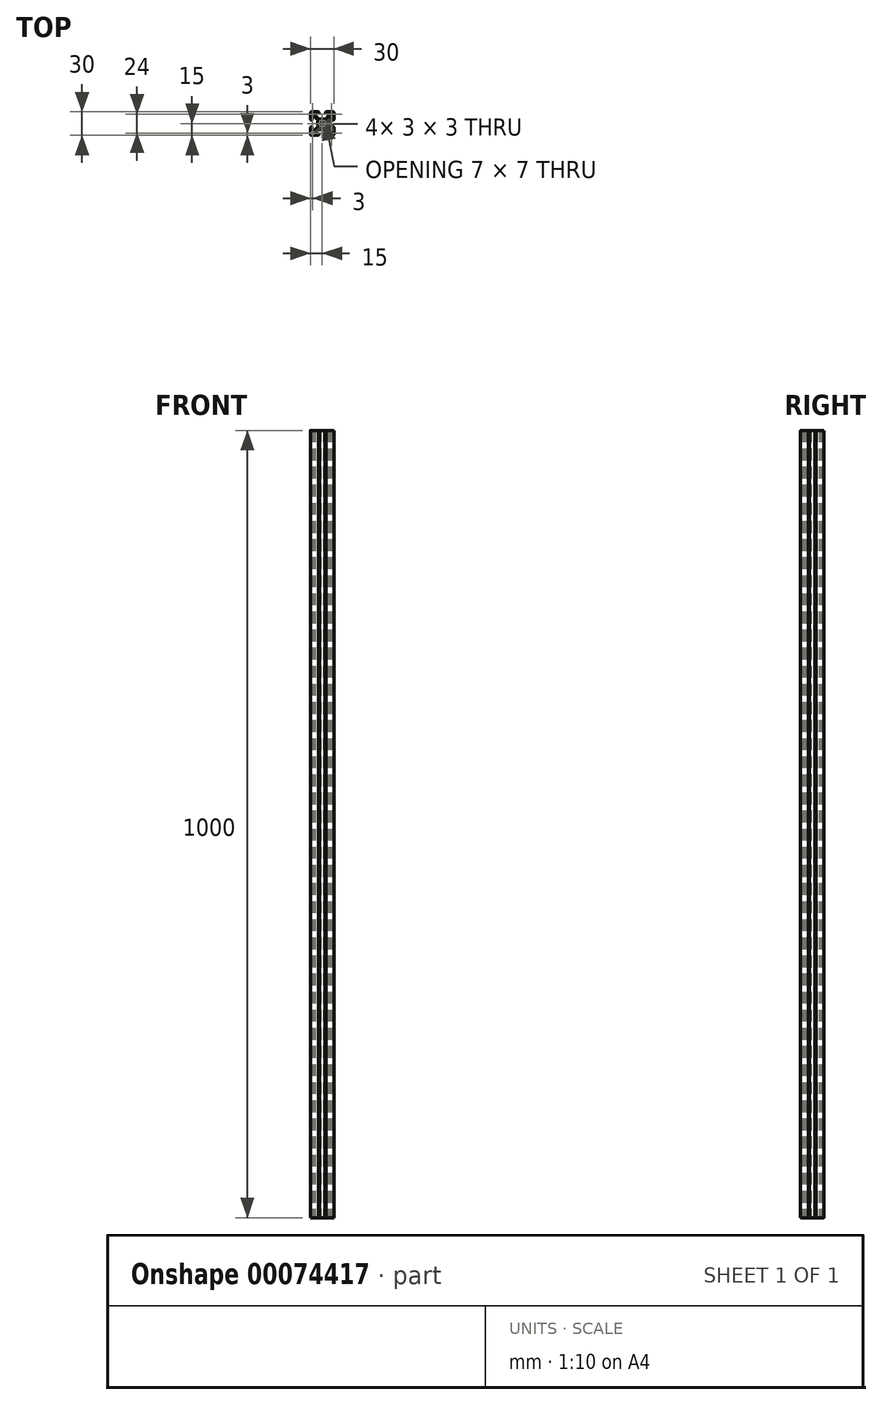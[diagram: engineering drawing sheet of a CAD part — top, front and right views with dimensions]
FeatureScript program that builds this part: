
annotation { "Feature Type Name" : "Feature", "Feature Type Description" : "" }
export const myFeature = defineFeature(function(context is Context, id is Id, definition is map)
    precondition{}
    {
        {
            var Q0;
            Q0=qCreatedBy(makeId("Top.planeOp"),FACE);
            var sketch = newSketch(context, id + "F0", { "sketchPlane" : qUnion([Q0])});
            skCircle(sketch, "E0", {"center": v(0, 0) * mm, "radius": 3.5 * mm});
            skLineSegment(sketch, "E1.bottom", {"start": v(-15, 15) * mm, "end": v(15, 15) * mm});
            skLineSegment(sketch, "E1.top", {"start": v(-15, -15) * mm, "end": v(15, -15) * mm});
            skLineSegment(sketch, "E1.left", {"start": v(-15, 15) * mm, "end": v(-15, -15) * mm});
            skLineSegment(sketch, "E1.right", {"start": v(15, 15) * mm, "end": v(15, -15) * mm});
            skLineSegment(sketch, "E2", {"start": v(-12.8, 12.8) * mm, "end": v(12.8, 12.8) * mm, "construction": true});
            skLineSegment(sketch, "E3", {"start": v(12.8, 12.8) * mm, "end": v(12.8, -12.8) * mm, "construction": true});
            skLineSegment(sketch, "E4", {"start": v(12.8, -12.8) * mm, "end": v(-12.8, -12.8) * mm, "construction": true});
            skLineSegment(sketch, "E5", {"start": v(-12.8, -12.8) * mm, "end": v(-12.8, 12.8) * mm, "construction": true});
            skLineSegment(sketch, "E6", {"start": v(-15, -15) * mm, "end": v(15, 15) * mm, "construction": true});
            skLineSegment(sketch, "E7", {"start": v(-15, 15) * mm, "end": v(15, -15) * mm, "construction": true});
            skLineSegment(sketch, "E8", {"start": v(-13.44, 15) * mm, "end": v(15, -13.44) * mm, "construction": true});
            skLineSegment(sketch, "E9", {"start": v(-15, 13.44) * mm, "end": v(13.44, -15) * mm, "construction": true});
            skLineSegment(sketch, "E10", {"start": v(13.44, 15) * mm, "end": v(-15, -13.44) * mm, "construction": true});
            skLineSegment(sketch, "E11", {"start": v(-13.44, -15) * mm, "end": v(15, 13.44) * mm, "construction": true});
            skLineSegment(sketch, "E12", {"start": v(-15, 4.1) * mm, "end": v(15, 4.1) * mm, "construction": true});
            skPoint(sketch, "E13.endSnap0", {"position": v(0.78, -0.78) * mm});
            skLineSegment(sketch, "E14", {"start": v(-4.1, 15) * mm, "end": v(-4.1, -15) * mm, "construction": true});
            skLineSegment(sketch, "E15", {"start": v(4.1, -15) * mm, "end": v(4.1, 15) * mm, "construction": true});
            skLineSegment(sketch, "E16", {"start": v(-15, -4.1) * mm, "end": v(15, -4.1) * mm, "construction": true});
            skLineSegment(sketch, "E17", {"start": v(-13.5, 13.5) * mm, "end": v(13.5, 13.5) * mm, "construction": true});
            skLineSegment(sketch, "E18", {"start": v(13.5, 13.5) * mm, "end": v(13.5, -13.5) * mm, "construction": true});
            skLineSegment(sketch, "E19", {"start": v(13.5, -13.5) * mm, "end": v(-13.5, -13.5) * mm, "construction": true});
            skLineSegment(sketch, "E20", {"start": v(-13.5, -13.5) * mm, "end": v(-13.5, 13.5) * mm, "construction": true});
            skLineSegment(sketch, "E21.bottom", {"start": v(-13.5, 13.5) * mm, "end": v(-10.5, 13.5) * mm});
            skLineSegment(sketch, "E21.top", {"start": v(-13.5, 10.5) * mm, "end": v(-10.5, 10.5) * mm});
            skLineSegment(sketch, "E21.left", {"start": v(-13.5, 13.5) * mm, "end": v(-13.5, 10.5) * mm});
            skLineSegment(sketch, "E21.right", {"start": v(-10.5, 13.5) * mm, "end": v(-10.5, 10.5) * mm});
            skLineSegment(sketch, "E22.bottom", {"start": v(13.5, 13.5) * mm, "end": v(10.5, 13.5) * mm});
            skLineSegment(sketch, "E22.top", {"start": v(13.5, 10.5) * mm, "end": v(10.5, 10.5) * mm});
            skLineSegment(sketch, "E22.left", {"start": v(13.5, 13.5) * mm, "end": v(13.5, 10.5) * mm});
            skLineSegment(sketch, "E22.right", {"start": v(10.5, 13.5) * mm, "end": v(10.5, 10.5) * mm});
            skLineSegment(sketch, "E23.bottom", {"start": v(13.5, -13.5) * mm, "end": v(10.5, -13.5) * mm});
            skLineSegment(sketch, "E23.top", {"start": v(13.5, -10.5) * mm, "end": v(10.5, -10.5) * mm});
            skLineSegment(sketch, "E23.left", {"start": v(13.5, -13.5) * mm, "end": v(13.5, -10.5) * mm});
            skLineSegment(sketch, "E23.right", {"start": v(10.5, -13.5) * mm, "end": v(10.5, -10.5) * mm});
            skLineSegment(sketch, "E24.bottom", {"start": v(-13.5, -13.5) * mm, "end": v(-10.5, -13.5) * mm});
            skLineSegment(sketch, "E24.top", {"start": v(-13.5, -10.5) * mm, "end": v(-10.5, -10.5) * mm});
            skLineSegment(sketch, "E24.left", {"start": v(-13.5, -13.5) * mm, "end": v(-13.5, -10.5) * mm});
            skLineSegment(sketch, "E24.right", {"start": v(-10.5, -13.5) * mm, "end": v(-10.5, -10.5) * mm});
            skLineSegment(sketch, "E25.bottom", {"start": v(13.5, 13.5) * mm, "end": v(9, 13.5) * mm, "construction": true});
            skLineSegment(sketch, "E25.top", {"start": v(13.5, 9) * mm, "end": v(9, 9) * mm, "construction": true});
            skLineSegment(sketch, "E25.left", {"start": v(13.5, 13.5) * mm, "end": v(13.5, 9) * mm, "construction": true});
            skLineSegment(sketch, "E25.right", {"start": v(9, 13.5) * mm, "end": v(9, 9) * mm, "construction": true});
            skLineSegment(sketch, "E26.bottom", {"start": v(-13.5, 13.5) * mm, "end": v(-9, 13.5) * mm, "construction": true});
            skLineSegment(sketch, "E26.top", {"start": v(-13.5, 9) * mm, "end": v(-9, 9) * mm, "construction": true});
            skLineSegment(sketch, "E26.left", {"start": v(-13.5, 13.5) * mm, "end": v(-13.5, 9) * mm, "construction": true});
            skLineSegment(sketch, "E26.right", {"start": v(-9, 13.5) * mm, "end": v(-9, 9) * mm, "construction": true});
            skLineSegment(sketch, "E27.bottom", {"start": v(-13.5, -13.5) * mm, "end": v(-9, -13.5) * mm, "construction": true});
            skLineSegment(sketch, "E27.top", {"start": v(-13.5, -9) * mm, "end": v(-9, -9) * mm, "construction": true});
            skLineSegment(sketch, "E27.left", {"start": v(-13.5, -13.5) * mm, "end": v(-13.5, -9) * mm, "construction": true});
            skLineSegment(sketch, "E27.right", {"start": v(-9, -13.5) * mm, "end": v(-9, -9) * mm, "construction": true});
            skLineSegment(sketch, "E28.bottom", {"start": v(13.5, -13.5) * mm, "end": v(9, -13.5) * mm, "construction": true});
            skLineSegment(sketch, "E28.top", {"start": v(13.5, -9) * mm, "end": v(9, -9) * mm, "construction": true});
            skLineSegment(sketch, "E28.left", {"start": v(13.5, -13.5) * mm, "end": v(13.5, -9) * mm, "construction": true});
            skLineSegment(sketch, "E28.right", {"start": v(9, -13.5) * mm, "end": v(9, -9) * mm, "construction": true});
            skCircle(sketch, "E29", {"center": v(0, 0) * mm, "radius": 6 * mm, "construction": true});
            skLineSegment(sketch, "E30", {"start": v(15, 4.1) * mm, "end": v(13.5, 4.1) * mm});
            skLineSegment(sketch, "E31", {"start": v(15, -4.1) * mm, "end": v(13.5, -4.1) * mm});
            skLineSegment(sketch, "E32", {"start": v(3.4, -4.95) * mm, "end": v(9, -10.56) * mm});
            skLineSegment(sketch, "E33", {"start": v(9, -10.56) * mm, "end": v(9, -12.8) * mm});
            skLineSegment(sketch, "E34", {"start": v(9, -12.8) * mm, "end": v(4.1, -12.8) * mm});
            skLineSegment(sketch, "E35", {"start": v(4.1, -12.8) * mm, "end": v(4.1, -15) * mm});
            skLineSegment(sketch, "E36", {"start": v(-4.1, -15) * mm, "end": v(-4.1, -12.8) * mm});
            skLineSegment(sketch, "E37", {"start": v(-4.1, -12.8) * mm, "end": v(-9, -12.8) * mm});
            skLineSegment(sketch, "E38", {"start": v(-9, -12.8) * mm, "end": v(-9, -10.56) * mm});
            skLineSegment(sketch, "E39", {"start": v(-9, -10.56) * mm, "end": v(-3.4, -4.95) * mm});
            skLineSegment(sketch, "E40", {"start": v(-4.95, -3.4) * mm, "end": v(-10.56, -9) * mm});
            skLineSegment(sketch, "E41", {"start": v(-10.56, -9) * mm, "end": v(-12.8, -9) * mm});
            skLineSegment(sketch, "E42", {"start": v(-12.8, -9) * mm, "end": v(-12.8, -4.1) * mm});
            skLineSegment(sketch, "E43", {"start": v(-12.8, -4.1) * mm, "end": v(-15, -4.1) * mm});
            skLineSegment(sketch, "E44", {"start": v(-15, 4.1) * mm, "end": v(-12.8, 4.1) * mm});
            skLineSegment(sketch, "E45", {"start": v(-12.8, 4.1) * mm, "end": v(-12.8, 9) * mm});
            skLineSegment(sketch, "E46", {"start": v(-12.8, 9) * mm, "end": v(-10.56, 9) * mm});
            skLineSegment(sketch, "E47", {"start": v(-10.56, 9) * mm, "end": v(-4.95, 3.4) * mm});
            skLineSegment(sketch, "E48", {"start": v(-4.1, 15) * mm, "end": v(-4.1, 12.8) * mm});
            skLineSegment(sketch, "E49", {"start": v(-4.1, 12.8) * mm, "end": v(-9, 12.8) * mm});
            skLineSegment(sketch, "E50", {"start": v(-9, 12.8) * mm, "end": v(-9, 10.56) * mm});
            skLineSegment(sketch, "E51", {"start": v(-9, 10.56) * mm, "end": v(-3.4, 4.95) * mm});
            skArc(sketch, "E52", {"start": v(-4.95, 3.4) * mm, "mid": v(-6, 0) * mm, "end": v(-4.95, -3.4) * mm});
            skArc(sketch, "E53", {"start": v(-3.4, -4.95) * mm, "mid": v(0, -6) * mm, "end": v(3.4, -4.95) * mm});
            skArc(sketch, "E54", {"start": v(3.4, 4.95) * mm, "mid": v(0, 6) * mm, "end": v(-3.4, 4.95) * mm});
            skLineSegment(sketch, "E55", {"start": v(4.1, 15) * mm, "end": v(4.1, 12.8) * mm});
            skLineSegment(sketch, "E56", {"start": v(4.1, 12.8) * mm, "end": v(9, 12.8) * mm});
            skLineSegment(sketch, "E57", {"start": v(9, 12.8) * mm, "end": v(9, 10.56) * mm});
            skLineSegment(sketch, "E58", {"start": v(9, 10.56) * mm, "end": v(3.4, 4.95) * mm});
            skLineSegment(sketch, "E59", {"start": v(13.5, 4.1) * mm, "end": v(12.8, 4.1) * mm});
            skLineSegment(sketch, "E60", {"start": v(13.5, -4.1) * mm, "end": v(12.8, -4.1) * mm});
            skLineSegment(sketch, "E61", {"start": v(4.95, 3.4) * mm, "end": v(10.56, 9) * mm});
            skLineSegment(sketch, "E62", {"start": v(10.56, 9) * mm, "end": v(12.8, 9) * mm});
            skLineSegment(sketch, "E63", {"start": v(12.8, 9) * mm, "end": v(12.8, 4.1) * mm});
            skLineSegment(sketch, "E64", {"start": v(10.56, -9) * mm, "end": v(12.8, -9) * mm});
            skLineSegment(sketch, "E65", {"start": v(12.8, -9) * mm, "end": v(12.8, -4.1) * mm});
            skLineSegment(sketch, "E66", {"start": v(4.95, -3.4) * mm, "end": v(10.56, -9) * mm});
            skArc(sketch, "E67", {"start": v(4.95, -3.4) * mm, "mid": v(6, 0) * mm, "end": v(4.95, 3.4) * mm});
            skCircle(sketch, "E68", {"center": v(0, 0) * mm, "radius": 4.25 * mm, "construction": true});
            skArc(sketch, "E69", {"start": v(3, 3) * mm, "mid": v(3.22, 2.43) * mm, "end": v(2.95, 1.9) * mm});
            skArc(sketch, "E70", {"start": v(3, 3) * mm, "mid": v(2.43, 3.22) * mm, "end": v(1.9, 2.95) * mm});
            skArc(sketch, "E71", {"start": v(-3, 3) * mm, "mid": v(-2.43, 3.22) * mm, "end": v(-1.9, 2.95) * mm});
            skArc(sketch, "E72", {"start": v(-3, 3) * mm, "mid": v(-3.22, 2.43) * mm, "end": v(-2.95, 1.9) * mm});
            skArc(sketch, "E73", {"start": v(-3, -3) * mm, "mid": v(-3.22, -2.43) * mm, "end": v(-2.95, -1.9) * mm});
            skArc(sketch, "E74", {"start": v(-3, -3) * mm, "mid": v(-2.43, -3.22) * mm, "end": v(-1.9, -2.95) * mm});
            skArc(sketch, "E75", {"start": v(3, -3) * mm, "mid": v(3.22, -2.43) * mm, "end": v(2.95, -1.9) * mm});
            skArc(sketch, "E76", {"start": v(3, -3) * mm, "mid": v(2.43, -3.22) * mm, "end": v(1.9, -2.95) * mm});
            skSolve(sketch);
        }
        {
            var Q0;
            Q0=makeQuery(id+"F0.imprint","IMPRINT",FACE,{"disambiguationData":[TD([[makeQuery(id+"F0.imprint","IMPRINT",EDGE,{"derivedFrom":sQuery(id+"F0.wireOp",EDGE,"E0")}),-1.0]])]});
            extrude(context, id + "F1", {"entities" : qUnion([Q0]), "depth" : 1000 * mm});
        }
        {
            var Q0;
            Q0=makeQuery(id+"F1.opExtrude","SWEPT_EDGE",EDGE,{"disambiguationData":[OSD([sQuery(id+"F0.wireOp",EDGE,"E1.bottom"),sQuery(id+"F0.wireOp",EDGE,"E1.right")])]});
            var Q1;
            Q1=makeQuery(id+"F1.opExtrude","SWEPT_EDGE",EDGE,{"disambiguationData":[OSD([sQuery(id+"F0.wireOp",EDGE,"E1.bottom"),sQuery(id+"F0.wireOp",EDGE,"E1.left")])]});
            var Q2;
            Q2=makeQuery(id+"F1.opExtrude","SWEPT_EDGE",EDGE,{"disambiguationData":[OSD([sQuery(id+"F0.wireOp",EDGE,"E1.top"),sQuery(id+"F0.wireOp",EDGE,"E1.right")])]});
            var Q3;
            Q3=makeQuery(id+"F1.opExtrude","SWEPT_EDGE",EDGE,{"disambiguationData":[OSD([sQuery(id+"F0.wireOp",EDGE,"E1.top"),sQuery(id+"F0.wireOp",EDGE,"E1.left")])]});
            fillet(context, id + "F2", {"entities" : qUnion([Q0, Q1, Q2, Q3]), "radius" : 1.5 * mm, "tangentPropagation" : true, "allowEdgeOverflow" : false});
        }
        {
            var Q0;
            Q0=makeQuery(id+"F1.opExtrude","SWEPT_EDGE",EDGE,{"disambiguationData":[OSD([sQuery(id+"F0.wireOp",EDGE,"E1.bottom"),sQuery(id+"F0.wireOp",EDGE,"E48")])]});
            var Q1;
            Q1=makeQuery(id+"F1.opExtrude","SWEPT_EDGE",EDGE,{"disambiguationData":[OSD([sQuery(id+"F0.wireOp",EDGE,"E1.bottom"),sQuery(id+"F0.wireOp",EDGE,"E55")])]});
            var Q2;
            Q2=makeQuery(id+"F1.opExtrude","SWEPT_EDGE",EDGE,{"disambiguationData":[OSD([sQuery(id+"F0.wireOp",EDGE,"E1.right"),sQuery(id+"F0.wireOp",EDGE,"E30")])]});
            var Q3;
            Q3=makeQuery(id+"F1.opExtrude","SWEPT_EDGE",EDGE,{"disambiguationData":[OSD([sQuery(id+"F0.wireOp",EDGE,"E1.right"),sQuery(id+"F0.wireOp",EDGE,"E31")])]});
            var Q4;
            Q4=makeQuery(id+"F1.opExtrude","SWEPT_EDGE",EDGE,{"disambiguationData":[OSD([sQuery(id+"F0.wireOp",EDGE,"E1.left"),sQuery(id+"F0.wireOp",EDGE,"E44")])]});
            var Q5;
            Q5=makeQuery(id+"F1.opExtrude","SWEPT_EDGE",EDGE,{"disambiguationData":[OSD([sQuery(id+"F0.wireOp",EDGE,"E1.left"),sQuery(id+"F0.wireOp",EDGE,"E43")])]});
            var Q6;
            Q6=makeQuery(id+"F1.opExtrude","SWEPT_EDGE",EDGE,{"disambiguationData":[OSD([sQuery(id+"F0.wireOp",EDGE,"E1.top"),sQuery(id+"F0.wireOp",EDGE,"E35")])]});
            var Q7;
            Q7=makeQuery(id+"F1.opExtrude","SWEPT_EDGE",EDGE,{"disambiguationData":[OSD([sQuery(id+"F0.wireOp",EDGE,"E1.top"),sQuery(id+"F0.wireOp",EDGE,"E36")])]});
            chamfer(context, id + "F3", {"entities" : qUnion([Q0, Q1, Q2, Q3, Q4, Q5, Q6, Q7]), "width" : 0.6 * mm, "tangentPropagation" : true});
        }
    });
